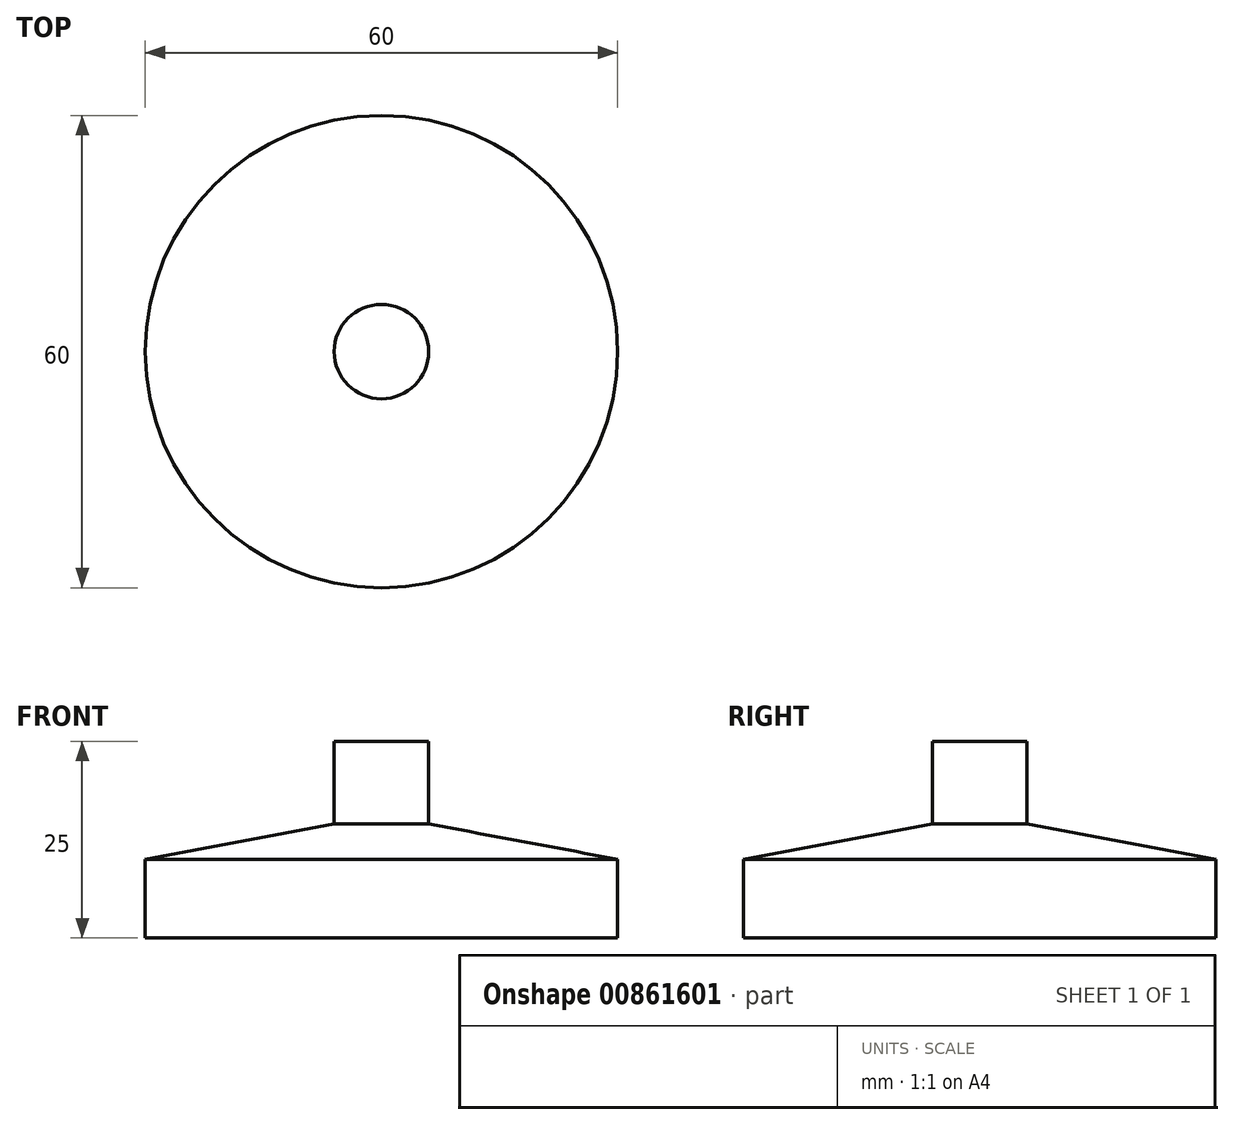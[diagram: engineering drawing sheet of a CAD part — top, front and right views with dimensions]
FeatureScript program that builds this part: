
annotation { "Feature Type Name" : "Feature", "Feature Type Description" : "" }
export const myFeature = defineFeature(function(context is Context, id is Id, definition is map)
    precondition{}
    {
        {
            var Q0;
            Q0=qCreatedBy(makeId("Front.planeOp"),FACE);
            var sketch = newSketch(context, id + "F0", { "sketchPlane" : qUnion([Q0])});
            skLineSegment(sketch, "E0", {"start": v(0, 0) * mm, "end": v(-30, 0) * mm});
            skLineSegment(sketch, "E1", {"start": v(-30, 0) * mm, "end": v(-30, 10) * mm});
            skLineSegment(sketch, "E2", {"start": v(-30, 10) * mm, "end": v(-6, 14.5) * mm});
            skLineSegment(sketch, "E3", {"start": v(-6, 14.5) * mm, "end": v(-6, 25) * mm});
            skLineSegment(sketch, "E4", {"start": v(-6, 25) * mm, "end": v(0, 25) * mm});
            skLineSegment(sketch, "E5", {"start": v(0, 25) * mm, "end": v(0, 0) * mm});
            skSolve(sketch);
        }
        {
            var Q0;
            Q0=makeQuery(id+"F0.imprint","IMPRINT",FACE,{"disambiguationData":[TD([[makeQuery(id+"F0.imprint","IMPRINT",EDGE,{"derivedFrom":sQuery(id+"F0.wireOp",EDGE,"E0")}),-1.0]])]});
            var Q1;
            Q1=sQuery(id+"F0.wireOp",EDGE,"E5");
            revolve(context, id + "F1", {"surfaceOperationType" : NewSurfaceOperationType.NEW, "entities" : qUnion([Q0]), "axis" : qUnion([Q1]), "revolveType" : RevolveType.FULL});
        }
    });
